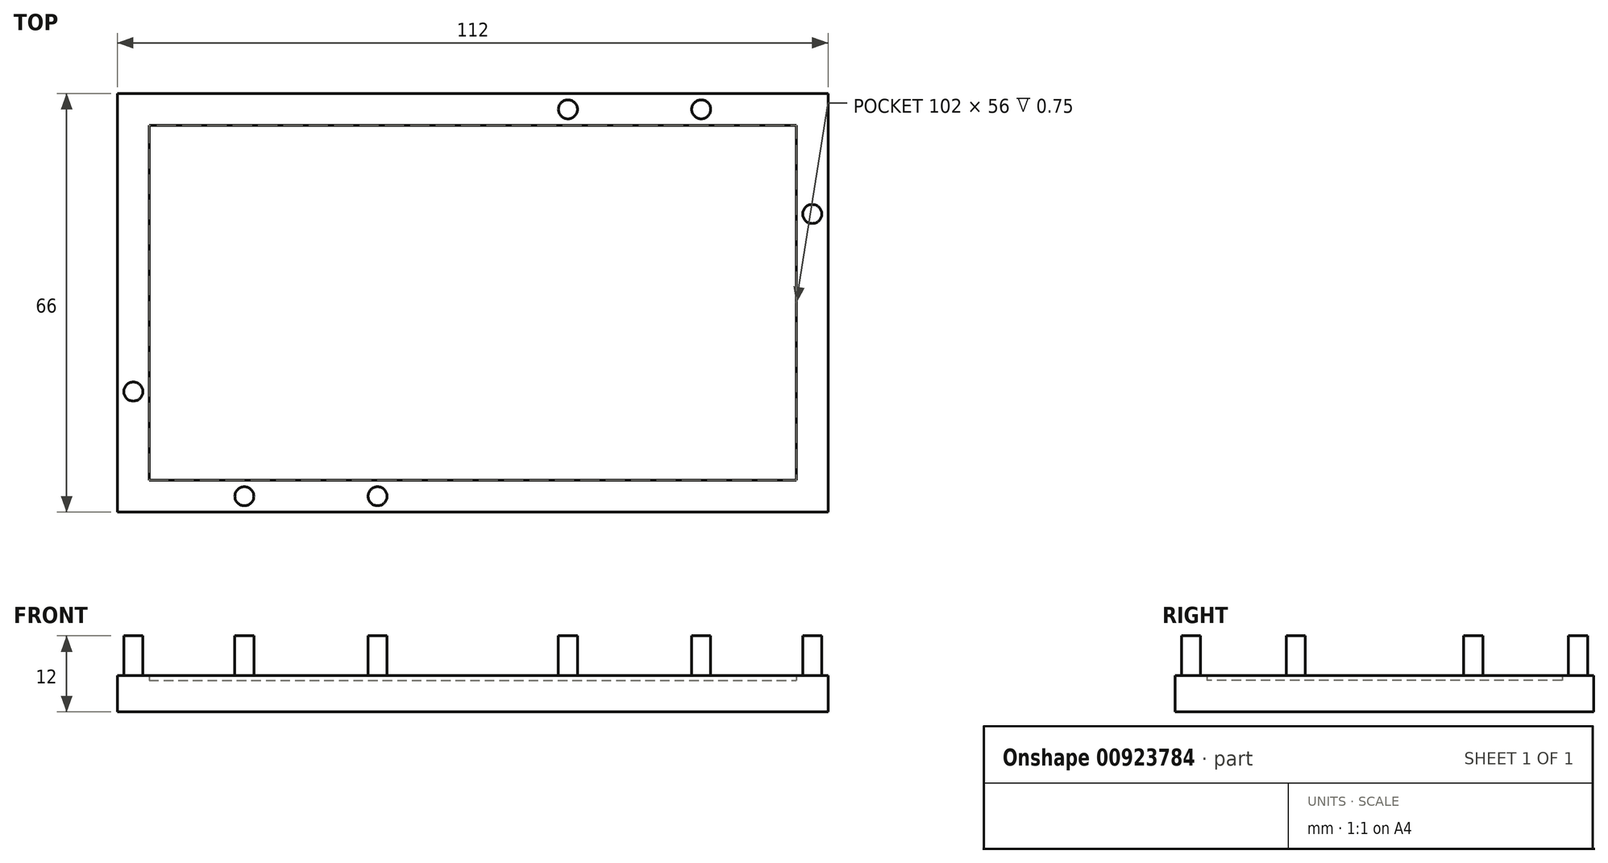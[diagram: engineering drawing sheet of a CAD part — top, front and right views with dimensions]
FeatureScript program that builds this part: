
annotation { "Feature Type Name" : "Feature", "Feature Type Description" : "" }
export const myFeature = defineFeature(function(context is Context, id is Id, definition is map)
    precondition{}
    {
        {
            var Q0;
            Q0=qCreatedBy(makeId("Top.planeOp"),FACE);
            var sketch = newSketch(context, id + "F0", { "sketchPlane" : qUnion([Q0])});
            skLineSegment(sketch, "E0.bottom", {"start": v(-56, 33) * mm, "end": v(56, 33) * mm});
            skLineSegment(sketch, "E0.top", {"start": v(-56, -33) * mm, "end": v(56, -33) * mm});
            skLineSegment(sketch, "E0.left", {"start": v(-56, 33) * mm, "end": v(-56, -33) * mm});
            skLineSegment(sketch, "E0.right", {"start": v(56, 33) * mm, "end": v(56, -33) * mm});
            skPoint(sketch, "E0.middle", {"position": v(0, 0) * mm});
            skSolve(sketch);
        }
        {
            var Q0;
            Q0 = qSketchRegion(id + "F0", true);
            extrude(context, id + "F1", {"entities" : qUnion([Q0]), "depth" : 12 * mm, "offsetDistance" : 25 * mm});
        }
        {
            var Q0;
            Q0=makeQuery(id+"F1.opExtrude","CAP_FACE",FACE,{"disambiguationData":[OSD([sQuery(id+"F0.wireOp",EDGE,"E0.bottom"),sQuery(id+"F0.wireOp",EDGE,"E0.top"),sQuery(id+"F0.wireOp",EDGE,"E0.left"),sQuery(id+"F0.wireOp",EDGE,"E0.right")])],"isStart":false});
            shell(context, id + "F2", {"entities" : qUnion([Q0]), "thickness" : 5 * mm});
        }
        {
            var Q0;
            Q0=makeQuery(id+"F1.opExtrude","CAP_FACE",FACE,{"disambiguationData":[OSD([sQuery(id+"F0.wireOp",EDGE,"E0.bottom"),sQuery(id+"F0.wireOp",EDGE,"E0.top"),sQuery(id+"F0.wireOp",EDGE,"E0.left"),sQuery(id+"F0.wireOp",EDGE,"E0.right")])],"isStart":false});
            var sketch = newSketch(context, id + "F3", { "sketchPlane" : qUnion([Q0])});
            skCircle(sketch, "E1", {"center": v(-36, 30.5) * mm, "radius": 1.5 * mm});
            skCircle(sketch, "E2", {"center": v(-15, 30.5) * mm, "radius": 1.5 * mm});
            skCircle(sketch, "E3.MirrorC", {"center": v(15, 30.5) * mm, "radius": 1.5 * mm});
            skCircle(sketch, "E4.MirrorC", {"center": v(36, 30.5) * mm, "radius": 1.5 * mm});
            skCircle(sketch, "E5.MirrorC", {"center": v(-36, -30.5) * mm, "radius": 1.5 * mm});
            skCircle(sketch, "E6.MirrorC", {"center": v(-15, -30.5) * mm, "radius": 1.5 * mm});
            skCircle(sketch, "E7.MirrorC", {"center": v(15, -30.5) * mm, "radius": 1.5 * mm});
            skCircle(sketch, "E8.MirrorC", {"center": v(36, -30.5) * mm, "radius": 1.5 * mm});
            skCircle(sketch, "E9", {"center": v(-53.5, 14) * mm, "radius": 1.5 * mm});
            skCircle(sketch, "E10.MirrorC", {"center": v(-53.5, -14) * mm, "radius": 1.5 * mm});
            skCircle(sketch, "E11.MirrorC", {"center": v(53.5, 14) * mm, "radius": 1.5 * mm});
            skCircle(sketch, "E12.MirrorC", {"center": v(53.5, -14) * mm, "radius": 1.5 * mm});
            skSolve(sketch);
        }
        {
            var Q0;
            Q0=makeQuery(id+"F3.imprint","IMPRINT",FACE,{"disambiguationData":[TD([[makeQuery(id+"F3.imprint","IMPRINT",EDGE,{"derivedFrom":sQuery(id+"F3.wireOp",EDGE,"E9")}),1.0]])]});
            var Q1;
            Q1=makeQuery(id+"F3.imprint","IMPRINT",FACE,{"disambiguationData":[TD([[makeQuery(id+"F3.imprint","IMPRINT",EDGE,{"derivedFrom":sQuery(id+"F3.wireOp",EDGE,"E10.MirrorC")}),-1.0]])]});
            var Q2;
            Q2=makeQuery(id+"F3.imprint","IMPRINT",FACE,{"disambiguationData":[TD([[makeQuery(id+"F3.imprint","IMPRINT",EDGE,{"derivedFrom":sQuery(id+"F3.wireOp",EDGE,"E1")}),1.0]])]});
            var Q3;
            Q3=makeQuery(id+"F3.imprint","IMPRINT",FACE,{"disambiguationData":[TD([[makeQuery(id+"F3.imprint","IMPRINT",EDGE,{"derivedFrom":sQuery(id+"F3.wireOp",EDGE,"E2")}),1.0]])]});
            var Q4;
            Q4=makeQuery(id+"F3.imprint","IMPRINT",FACE,{"disambiguationData":[TD([[makeQuery(id+"F3.imprint","IMPRINT",EDGE,{"derivedFrom":sQuery(id+"F3.wireOp",EDGE,"E3.MirrorC")}),-1.0]])]});
            var Q5;
            Q5=makeQuery(id+"F3.imprint","IMPRINT",FACE,{"disambiguationData":[TD([[makeQuery(id+"F3.imprint","IMPRINT",EDGE,{"derivedFrom":sQuery(id+"F3.wireOp",EDGE,"E4.MirrorC")}),-1.0]])]});
            var Q6;
            Q6=makeQuery(id+"F3.imprint","IMPRINT",FACE,{"disambiguationData":[TD([[makeQuery(id+"F3.imprint","IMPRINT",EDGE,{"derivedFrom":sQuery(id+"F3.wireOp",EDGE,"E11.MirrorC")}),-1.0]])]});
            var Q7;
            Q7=makeQuery(id+"F3.imprint","IMPRINT",FACE,{"disambiguationData":[TD([[makeQuery(id+"F3.imprint","IMPRINT",EDGE,{"derivedFrom":sQuery(id+"F3.wireOp",EDGE,"E12.MirrorC")}),1.0]])]});
            var Q8;
            Q8=makeQuery(id+"F3.imprint","IMPRINT",FACE,{"disambiguationData":[TD([[makeQuery(id+"F3.imprint","IMPRINT",EDGE,{"derivedFrom":sQuery(id+"F3.wireOp",EDGE,"E8.MirrorC")}),1.0]])]});
            var Q9;
            Q9=makeQuery(id+"F3.imprint","IMPRINT",FACE,{"disambiguationData":[TD([[makeQuery(id+"F3.imprint","IMPRINT",EDGE,{"derivedFrom":sQuery(id+"F3.wireOp",EDGE,"E7.MirrorC")}),1.0]])]});
            var Q10;
            Q10=makeQuery(id+"F3.imprint","IMPRINT",FACE,{"disambiguationData":[TD([[makeQuery(id+"F3.imprint","IMPRINT",EDGE,{"derivedFrom":sQuery(id+"F3.wireOp",EDGE,"E6.MirrorC")}),-1.0]])]});
            var Q11;
            Q11=makeQuery(id+"F3.imprint","IMPRINT",FACE,{"disambiguationData":[TD([[makeQuery(id+"F3.imprint","IMPRINT",EDGE,{"derivedFrom":sQuery(id+"F3.wireOp",EDGE,"E5.MirrorC")}),-1.0]])]});
            extrude(context, id + "F4", {"entities" : qUnion([Q0, Q1, Q2, Q3, Q4, Q5, Q6, Q7, Q8, Q9, Q10, Q11]), "operationType" : NewBodyOperationType.REMOVE, "oppositeDirection" : true, "depth" : 6.25 * mm, "offsetDistance" : 25 * mm});
        }
    });
